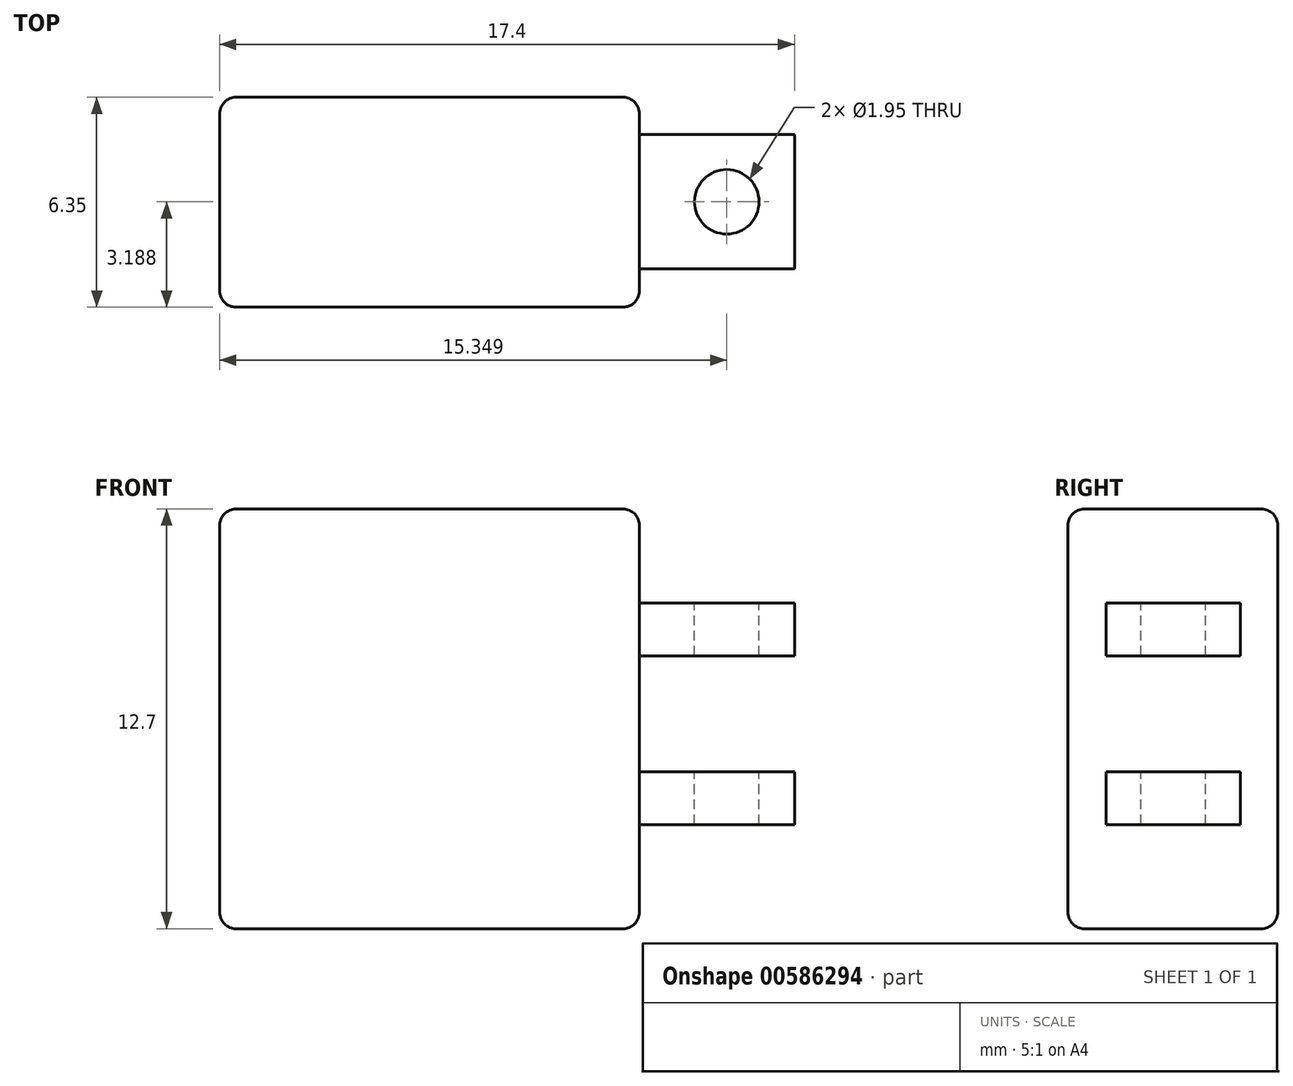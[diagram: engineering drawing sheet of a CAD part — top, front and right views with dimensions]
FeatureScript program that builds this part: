
annotation { "Feature Type Name" : "Feature", "Feature Type Description" : "" }
export const myFeature = defineFeature(function(context is Context, id is Id, definition is map)
    precondition{}
    {
        {
            var Q0;
            Q0=qCreatedBy(makeId("Front.planeOp"),FACE);
            var sketch = newSketch(context, id + "F0", { "sketchPlane" : qUnion([Q0])});
            skLineSegment(sketch, "E0.bottom", {"start": v(-5.2, 6.2) * mm, "end": v(7.5, 6.2) * mm});
            skLineSegment(sketch, "E0.top", {"start": v(-5.2, -6.5) * mm, "end": v(7.5, -6.5) * mm});
            skLineSegment(sketch, "E0.left", {"start": v(-5.2, 6.2) * mm, "end": v(-5.2, -6.5) * mm});
            skLineSegment(sketch, "E0.right", {"start": v(7.5, 6.2) * mm, "end": v(7.5, -6.5) * mm});
            skSolve(sketch);
        }
        {
            var Q0;
            Q0=makeQuery(id+"F0.imprint","IMPRINT",FACE,{"disambiguationData":[TD([[makeQuery(id+"F0.imprint","IMPRINT",EDGE,{"derivedFrom":sQuery(id+"F0.wireOp",EDGE,"E0.bottom")}),-1.0]])]});
            extrude(context, id + "F1", {"entities" : qUnion([Q0]), "depth" : 6.35 * mm, "offsetDistance" : 25.4 * mm});
        }
        {
            var Q0;
            Q0=makeQuery(id+"F1.opExtrude","SWEPT_FACE",FACE,{"disambiguationData":[OSD([sQuery(id+"F0.wireOp",EDGE,"E0.right")])]});
            var sketch = newSketch(context, id + "F2", { "sketchPlane" : qUnion([Q0])});
            skLineSegment(sketch, "E1.bottom", {"start": v(-5.2, 3.35) * mm, "end": v(-1.13, 3.35) * mm});
            skLineSegment(sketch, "E1.top", {"start": v(-5.2, 1.76) * mm, "end": v(-1.13, 1.76) * mm});
            skLineSegment(sketch, "E1.left", {"start": v(-5.2, 3.35) * mm, "end": v(-5.2, 1.76) * mm});
            skLineSegment(sketch, "E1.right", {"start": v(-1.13, 3.35) * mm, "end": v(-1.13, 1.76) * mm});
            skLineSegment(sketch, "E2", {"start": v(-6.35, 0) * mm, "end": v(0, 0) * mm});
            skLineSegment(sketch, "E3.MirrorCS", {"start": v(-5.2, -1.76) * mm, "end": v(-1.13, -1.76) * mm});
            skLineSegment(sketch, "E4.MirrorCS", {"start": v(-5.2, -3.35) * mm, "end": v(-1.13, -3.35) * mm});
            skLineSegment(sketch, "E5.MirrorCS", {"start": v(-1.13, -3.35) * mm, "end": v(-1.13, -1.76) * mm});
            skLineSegment(sketch, "E6.MirrorCS", {"start": v(-5.2, -3.35) * mm, "end": v(-5.2, -1.76) * mm});
            skSolve(sketch);
        }
        {
            var Q0;
            Q0=makeQuery(id+"F2.imprint","IMPRINT",FACE,{"disambiguationData":[TD([[makeQuery(id+"F2.imprint","IMPRINT",EDGE,{"derivedFrom":sQuery(id+"F2.wireOp",EDGE,"E1.bottom")}),-1.0]])]});
            var sketch = newSketch(context, id + "F3", { "sketchPlane" : qUnion([Q0])});
            skSolve(sketch);
        }
        {
            var Q0;
            Q0 = qSketchRegion(id + "F3", true);
            var Q1;
            Q1=makeQuery(id+"F2.imprint","IMPRINT",FACE,{"disambiguationData":[TD([[makeQuery(id+"F2.imprint","IMPRINT",EDGE,{"derivedFrom":sQuery(id+"F2.wireOp",EDGE,"E1.bottom")}),-1.0]])]});
            var Q2;
            Q2=makeQuery(id+"F2.imprint","IMPRINT",FACE,{"disambiguationData":[TD([[makeQuery(id+"F2.imprint","IMPRINT",EDGE,{"derivedFrom":sQuery(id+"F2.wireOp",EDGE,"E3.MirrorCS")}),-1.0]])]});
            extrude(context, id + "F4", {"entities" : qUnion([Q0, Q1, Q2]), "operationType" : NewBodyOperationType.ADD, "depth" : 4.7 * mm, "offsetDistance" : 25.4 * mm});
        }
        {
            var Q0;
            Q0=makeQuery(id+"F4.opExtrude","SWEPT_FACE",FACE,{"disambiguationData":[OSD([sQuery(id+"F2.wireOp",EDGE,"E1.bottom")])]});
            var sketch = newSketch(context, id + "F5", { "sketchPlane" : qUnion([Q0])});
            skCircle(sketch, "E7", {"center": v(10.14, -3.16) * mm, "radius": 0.98 * mm});
            skPoint(sketch, "E7.centerSnap0", {"position": v(12.2, -3.16) * mm});
            skSolve(sketch);
        }
        {
            var Q0;
            Q0=makeQuery(id+"F5.imprint","IMPRINT",FACE,{"disambiguationData":[TD([[makeQuery(id+"F5.imprint","IMPRINT",EDGE,{"derivedFrom":sQuery(id+"F5.wireOp",EDGE,"E7")}),1.0]])]});
            extrude(context, id + "F6", {"entities" : qUnion([Q0]), "operationType" : NewBodyOperationType.REMOVE, "oppositeDirection" : true, "depth" : 25.4 * mm, "offsetDistance" : 25.4 * mm});
        }
        {
            var Q0;
            Q0=makeQuery(id+"F1.opExtrude","CAP_EDGE",EDGE,{"disambiguationData":[OSD([sQuery(id+"F0.wireOp",EDGE,"E0.bottom")])],"isStart":true});
            var Q1;
            Q1=makeQuery(id+"F1.opExtrude","CAP_EDGE",EDGE,{"disambiguationData":[OSD([sQuery(id+"F0.wireOp",EDGE,"E0.right")])],"isStart":true});
            var Q2;
            Q2=makeQuery(id+"F1.opExtrude","SWEPT_EDGE",EDGE,{"disambiguationData":[OSD([sQuery(id+"F0.wireOp",EDGE,"E0.bottom"),sQuery(id+"F0.wireOp",EDGE,"E0.right")])]});
            var Q3;
            Q3=makeQuery(id+"F1.opExtrude","CAP_EDGE",EDGE,{"disambiguationData":[OSD([sQuery(id+"F0.wireOp",EDGE,"E0.bottom")])],"isStart":false});
            var Q4;
            Q4=makeQuery(id+"F1.opExtrude","SWEPT_EDGE",EDGE,{"disambiguationData":[OSD([sQuery(id+"F0.wireOp",EDGE,"E0.bottom"),sQuery(id+"F0.wireOp",EDGE,"E0.left")])]});
            var Q5;
            Q5=makeQuery(id+"F1.opExtrude","CAP_EDGE",EDGE,{"disambiguationData":[OSD([sQuery(id+"F0.wireOp",EDGE,"E0.right")])],"isStart":false});
            var Q6;
            Q6=makeQuery(id+"F1.opExtrude","SWEPT_EDGE",EDGE,{"disambiguationData":[OSD([sQuery(id+"F0.wireOp",EDGE,"E0.top"),sQuery(id+"F0.wireOp",EDGE,"E0.right")])]});
            var Q7;
            Q7=makeQuery(id+"F1.opExtrude","CAP_EDGE",EDGE,{"disambiguationData":[OSD([sQuery(id+"F0.wireOp",EDGE,"E0.left")])],"isStart":true});
            var Q8;
            Q8=makeQuery(id+"F1.opExtrude","CAP_EDGE",EDGE,{"disambiguationData":[OSD([sQuery(id+"F0.wireOp",EDGE,"E0.top")])],"isStart":true});
            var Q9;
            Q9=makeQuery(id+"F1.opExtrude","CAP_EDGE",EDGE,{"disambiguationData":[OSD([sQuery(id+"F0.wireOp",EDGE,"E0.left")])],"isStart":false});
            var Q10;
            Q10=makeQuery(id+"F1.opExtrude","SWEPT_EDGE",EDGE,{"disambiguationData":[OSD([sQuery(id+"F0.wireOp",EDGE,"E0.top"),sQuery(id+"F0.wireOp",EDGE,"E0.left")])]});
            var Q11;
            Q11=makeQuery(id+"F1.opExtrude","CAP_EDGE",EDGE,{"disambiguationData":[OSD([sQuery(id+"F0.wireOp",EDGE,"E0.top")])],"isStart":false});
            fillet(context, id + "F7", {"entities" : qUnion([Q0, Q1, Q2, Q3, Q4, Q5, Q6, Q7, Q8, Q9, Q10, Q11]), "radius" : 0.5 * mm, "tangentPropagation" : true, "allowEdgeOverflow" : false});
        }
    });
